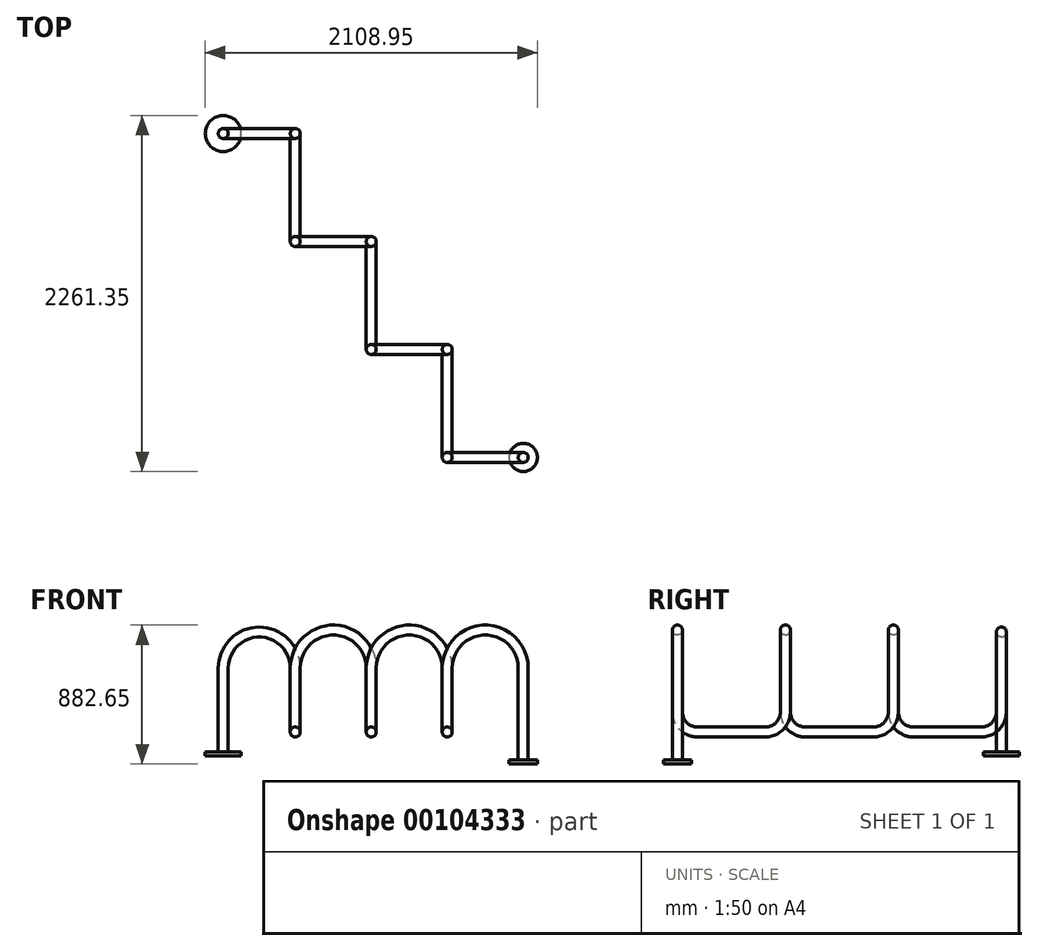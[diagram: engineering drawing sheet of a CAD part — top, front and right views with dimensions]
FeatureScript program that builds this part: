
annotation { "Feature Type Name" : "Feature", "Feature Type Description" : "" }
export const myFeature = defineFeature(function(context is Context, id is Id, definition is map)
    precondition{}
    {
        {
            var Q0;
            Q0=qCreatedBy(makeId("Front.planeOp"),FACE);
            var sketch = newSketch(context, id + "F0", { "sketchPlane" : qUnion([Q0])});
            skLineSegment(sketch, "E0", {"start": v(0, 0) * mm, "end": v(0, -152.4) * mm});
            skLineSegment(sketch, "E1", {"start": v(0, 0) * mm, "end": v(0, 406.4) * mm});
            skArc(sketch, "E2", {"start": v(457.2, 406.4) * mm, "mid": v(228.6, 635) * mm, "end": v(0, 406.4) * mm});
            skSolve(sketch);
        }
        {
            var Q0;
            Q0=sQuery(id+"F0.wireOp",VERTEX,"E2.start");
            var Q1;
            Q1=qCreatedBy(makeId("Right.planeOp"),FACE);
            cPlane(context, id + "F1", {"entities" : qUnion([Q0, Q1]), "cplaneType" : CPlaneType.PLANE_POINT, "offset" : 152.4 * mm, "width" : 152.4 * mm, "height" : 152.4 * mm});
        }
        {
            var Q0;
            Q0=qCreatedBy(id+"F1.planeOp",FACE);
            var sketch = newSketch(context, id + "F2", { "sketchPlane" : qUnion([Q0])});
            skLineSegment(sketch, "E3", {"start": v(0, 406.4) * mm, "end": v(0, 127) * mm});
            skLineSegment(sketch, "E4", {"start": v(-127, 0) * mm, "end": v(-558.8, 0) * mm});
            skLineSegment(sketch, "E5", {"start": v(-685.8, 127) * mm, "end": v(-685.8, 406.4) * mm});
            skPoint(sketch, "E6.visualSharp", {"position": v(-685.8, 0) * mm});
            skArc(sketch, "E6.filletArc", {"start": v(-685.8, 127) * mm, "mid": v(-648.6, 37.2) * mm, "end": v(-558.8, 0) * mm});
            skPoint(sketch, "E7.visualSharp", {"position": v(0, 0) * mm});
            skArc(sketch, "E7.filletArc", {"start": v(-127, 0) * mm, "mid": v(-37.2, 37.2) * mm, "end": v(0, 127) * mm});
            skSolve(sketch);
        }
        {
            var Q0;
            Q0=sQuery(id+"F2.wireOp",VERTEX,"E5.end");
            var Q1;
            Q1=qCreatedBy(makeId("Front.planeOp"),FACE);
            cPlane(context, id + "F3", {"entities" : qUnion([Q0, Q1]), "cplaneType" : CPlaneType.PLANE_POINT, "offset" : 152.4 * mm, "width" : 152.4 * mm, "height" : 152.4 * mm});
        }
        {
            var Q0;
            Q0=qCreatedBy(id+"F3.planeOp",FACE);
            var sketch = newSketch(context, id + "F4", { "sketchPlane" : qUnion([Q0])});
            skArc(sketch, "E8", {"start": v(939.8, 406.4) * mm, "mid": v(698.5, 647.7) * mm, "end": v(457.2, 406.4) * mm});
            skSolve(sketch);
        }
        {
            var Q0;
            Q0=sQuery(id+"F4.wireOp",VERTEX,"E8.start");
            var Q1;
            Q1=qCreatedBy(makeId("Right.planeOp"),FACE);
            cPlane(context, id + "F5", {"entities" : qUnion([Q0, Q1]), "cplaneType" : CPlaneType.PLANE_POINT, "offset" : 152.4 * mm, "width" : 152.4 * mm, "height" : 152.4 * mm});
        }
        {
            var Q0;
            Q0=qCreatedBy(id+"F5.planeOp",FACE);
            var sketch = newSketch(context, id + "F6", { "sketchPlane" : qUnion([Q0])});
            skLineSegment(sketch, "E9", {"start": v(-1371.6, 406.4) * mm, "end": v(-1371.6, 127) * mm});
            skLineSegment(sketch, "E10", {"start": v(-1244.6, 0) * mm, "end": v(-812.8, 0) * mm});
            skLineSegment(sketch, "E11", {"start": v(-685.8, 127) * mm, "end": v(-685.8, 406.4) * mm});
            skPoint(sketch, "E12.visualSharp", {"position": v(-1371.6, 0) * mm});
            skArc(sketch, "E12.filletArc", {"start": v(-1371.6, 127) * mm, "mid": v(-1334.4, 37.2) * mm, "end": v(-1244.6, 0) * mm});
            skPoint(sketch, "E13.visualSharp", {"position": v(-685.8, 0) * mm});
            skArc(sketch, "E13.filletArc", {"start": v(-812.8, 0) * mm, "mid": v(-723, 37.2) * mm, "end": v(-685.8, 127) * mm});
            skSolve(sketch);
        }
        {
            var Q0;
            Q0=sQuery(id+"F6.wireOp",VERTEX,"E9.start");
            var Q1;
            Q1=qCreatedBy(makeId("Front.planeOp"),FACE);
            cPlane(context, id + "F7", {"entities" : qUnion([Q0, Q1]), "cplaneType" : CPlaneType.PLANE_POINT, "offset" : 152.4 * mm, "width" : 152.4 * mm, "height" : 152.4 * mm});
        }
        {
            var Q0;
            Q0=qCreatedBy(id+"F7.planeOp",FACE);
            var sketch = newSketch(context, id + "F8", { "sketchPlane" : qUnion([Q0])});
            skArc(sketch, "E14", {"start": v(1422.4, 406.4) * mm, "mid": v(1181.1, 647.7) * mm, "end": v(939.8, 406.4) * mm});
            skSolve(sketch);
        }
        {
            var Q0;
            Q0=sQuery(id+"F8.wireOp",VERTEX,"E14.start");
            var Q1;
            Q1=qCreatedBy(makeId("Right.planeOp"),FACE);
            cPlane(context, id + "F9", {"entities" : qUnion([Q0, Q1]), "cplaneType" : CPlaneType.PLANE_POINT, "offset" : 152.4 * mm, "width" : 152.4 * mm, "height" : 152.4 * mm});
        }
        {
            var Q0;
            Q0=qCreatedBy(id+"F9.planeOp",FACE);
            var sketch = newSketch(context, id + "F10", { "sketchPlane" : qUnion([Q0])});
            skLineSegment(sketch, "E15", {"start": v(-1371.6, 406.4) * mm, "end": v(-1371.6, 127) * mm});
            skLineSegment(sketch, "E16", {"start": v(-1498.6, 0) * mm, "end": v(-1930.4, 0) * mm});
            skLineSegment(sketch, "E17", {"start": v(-2057.4, 127) * mm, "end": v(-2057.4, 406.4) * mm});
            skPoint(sketch, "E18.visualSharp", {"position": v(-1371.6, 0) * mm});
            skArc(sketch, "E18.filletArc", {"start": v(-1498.6, 0) * mm, "mid": v(-1408.8, 37.2) * mm, "end": v(-1371.6, 127) * mm});
            skPoint(sketch, "E19.visualSharp", {"position": v(-2057.4, 0) * mm});
            skArc(sketch, "E19.filletArc", {"start": v(-2057.4, 127) * mm, "mid": v(-2020.2, 37.2) * mm, "end": v(-1930.4, 0) * mm});
            skSolve(sketch);
        }
        {
            var Q0;
            Q0=sQuery(id+"F10.wireOp",VERTEX,"E17.end");
            var Q1;
            Q1=qCreatedBy(makeId("Front.planeOp"),FACE);
            var Q2;
            Q2 = qBodyType(qCreatedBy(id + "F12" ,EDGE), BodyType.WIRE);
            cPlane(context, id + "F11", {"entities" : qUnion([Q0, Q1, Q2]), "cplaneType" : CPlaneType.PLANE_POINT, "offset" : 152.4 * mm, "width" : 152.4 * mm, "height" : 152.4 * mm});
        }
        {
            var Q0;
            Q0=qCreatedBy(id+"F11.planeOp",FACE);
            var sketch = newSketch(context, id + "F12", { "sketchPlane" : qUnion([Q0])});
            skArc(sketch, "E20", {"start": v(1905, 406.4) * mm, "mid": v(1663.7, 647.7) * mm, "end": v(1422.4, 406.4) * mm});
            skLineSegment(sketch, "E21", {"start": v(1905, 406.4) * mm, "end": v(1905, -203.2) * mm});
            skSolve(sketch);
        }
        {
            var Q0;
            Q0=sQuery(id+"F12.wireOp",VERTEX,"E21.end");
            var Q1;
            Q1=qCreatedBy(makeId("Top.planeOp"),FACE);
            cPlane(context, id + "F13", {"entities" : qUnion([Q0, Q1]), "cplaneType" : CPlaneType.PLANE_POINT, "offset" : 152.4 * mm, "width" : 152.4 * mm, "height" : 152.4 * mm});
        }
        {
            var Q0;
            Q0=sQuery(id+"F0.wireOp",VERTEX,"E0.end");
            var Q1;
            Q1=qCreatedBy(makeId("Top.planeOp"),FACE);
            cPlane(context, id + "F14", {"entities" : qUnion([Q0, Q1]), "cplaneType" : CPlaneType.PLANE_POINT, "offset" : 152.4 * mm, "width" : 152.4 * mm, "height" : 152.4 * mm});
        }
        {
            var Q0;
            Q0=qCreatedBy(id+"F14.planeOp",FACE);
            var sketch = newSketch(context, id + "F15", { "sketchPlane" : qUnion([Q0])});
            skCircle(sketch, "E22", {"center": v(0, 0) * mm, "radius": 31.75 * mm});
            skCircle(sketch, "E23", {"center": v(0, 0) * mm, "radius": 114.3 * mm});
            skSolve(sketch);
        }
        {
            var Q0;
            Q0=makeQuery(id+"F15.imprint","IMPRINT",FACE,{"disambiguationData":[TD([[makeQuery(id+"F15.imprint","IMPRINT",EDGE,{"derivedFrom":sQuery(id+"F15.wireOp",EDGE,"E22")}),1.0]])]});
            var Q1;
            Q1=sQuery(id+"F0.wireOp",EDGE,"E0");
            var Q2;
            Q2=sQuery(id+"F0.wireOp",EDGE,"E1");
            var Q3;
            Q3=sQuery(id+"F0.wireOp",EDGE,"E2");
            var Q4;
            Q4=sQuery(id+"F2.wireOp",EDGE,"E3");
            var Q5;
            Q5=sQuery(id+"F2.wireOp",EDGE,"E7.filletArc");
            var Q6;
            Q6=sQuery(id+"F2.wireOp",EDGE,"E4");
            var Q7;
            Q7=sQuery(id+"F2.wireOp",EDGE,"E6.filletArc");
            var Q8;
            Q8=sQuery(id+"F2.wireOp",EDGE,"E5");
            var Q9;
            Q9=sQuery(id+"F4.wireOp",EDGE,"E8");
            var Q10;
            Q10=sQuery(id+"F6.wireOp",EDGE,"E11");
            var Q11;
            Q11=sQuery(id+"F6.wireOp",EDGE,"E13.filletArc");
            var Q12;
            Q12=sQuery(id+"F6.wireOp",EDGE,"E10");
            var Q13;
            Q13=sQuery(id+"F6.wireOp",EDGE,"E12.filletArc");
            var Q14;
            Q14=sQuery(id+"F6.wireOp",EDGE,"E9");
            var Q15;
            Q15=sQuery(id+"F8.wireOp",EDGE,"E14");
            var Q16;
            Q16=sQuery(id+"F10.wireOp",EDGE,"E15");
            var Q17;
            Q17=sQuery(id+"F10.wireOp",EDGE,"E18.filletArc");
            var Q18;
            Q18=sQuery(id+"F10.wireOp",EDGE,"E16");
            var Q19;
            Q19=sQuery(id+"F10.wireOp",EDGE,"E19.filletArc");
            var Q20;
            Q20=sQuery(id+"F10.wireOp",EDGE,"E17");
            var Q21;
            Q21=sQuery(id+"F12.wireOp",EDGE,"E20");
            var Q22;
            Q22=sQuery(id+"F12.wireOp",EDGE,"E21");
            var Q23;
            Q23=sQuery(id+"F10.wireOp",EDGE,"E17");
            sweep(context, id + "F16", {"profiles" : qUnion([Q0]), "path" : qUnion([Q1, Q2, Q3, Q4, Q5, Q6, Q7, Q8, Q9, Q10, Q11, Q12, Q13, Q14, Q15, Q16, Q17, Q18, Q19, Q20, Q21, Q22, Q23])});
        }
        {
            var Q0;
            Q0=makeQuery(id+"F15.imprint","IMPRINT",FACE,{"disambiguationData":[TD([[makeQuery(id+"F15.imprint","IMPRINT",EDGE,{"derivedFrom":sQuery(id+"F15.wireOp",EDGE,"E22")}),-1.0]])]});
            extrude(context, id + "F17", {"entities" : qUnion([Q0]), "operationType" : NewBodyOperationType.ADD, "depth" : 25.4 * mm});
        }
        {
            var Q0;
            Q0=qCreatedBy(id+"F13.planeOp",FACE);
            var sketch = newSketch(context, id + "F18", { "sketchPlane" : qUnion([Q0])});
            skPoint(sketch, "E24.0", {"position": v(1905, -2057.4) * mm});
            skCircle(sketch, "E25", {"center": v(1905, -2057.4) * mm, "radius": 89.65 * mm});
            skSolve(sketch);
        }
        {
            var Q0;
            Q0=makeQuery(id+"F18.imprint","IMPRINT",FACE,{"disambiguationData":[TD([[makeQuery(id+"F18.imprint","IMPRINT",EDGE,{"derivedFrom":sQuery(id+"F18.wireOp",EDGE,"E25")}),1.0]])]});
            extrude(context, id + "F19", {"entities" : qUnion([Q0]), "operationType" : NewBodyOperationType.ADD, "depth" : 25.4 * mm});
        }
    });
